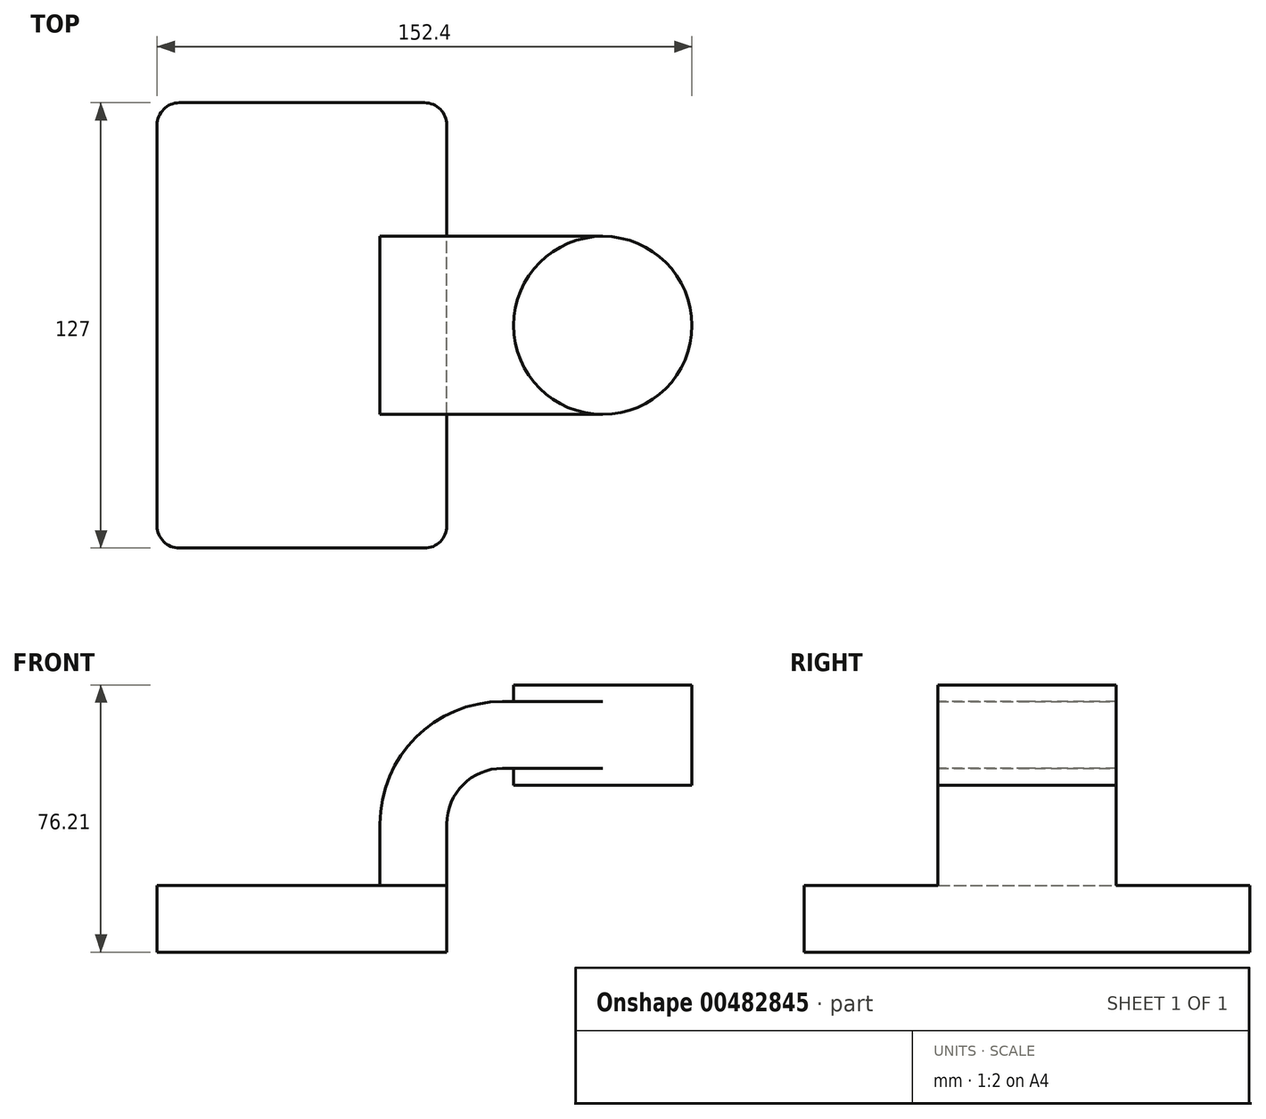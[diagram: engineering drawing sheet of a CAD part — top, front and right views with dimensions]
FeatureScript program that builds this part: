
annotation { "Feature Type Name" : "Feature", "Feature Type Description" : "" }
export const myFeature = defineFeature(function(context is Context, id is Id, definition is map)
    precondition{}
    {
        {
            var Q0;
            Q0=qCreatedBy(makeId("Front.planeOp"),FACE);
            var sketch = newSketch(context, id + "F0", { "sketchPlane" : qUnion([Q0])});
            skLineSegment(sketch, "E0.bottom", {"start": v(-41.28, -9.53) * mm, "end": v(41.28, -9.53) * mm});
            skLineSegment(sketch, "E0.top", {"start": v(-41.28, 9.53) * mm, "end": v(41.28, 9.53) * mm});
            skLineSegment(sketch, "E0.left", {"start": v(-41.28, -9.53) * mm, "end": v(-41.28, 9.53) * mm});
            skLineSegment(sketch, "E0.right", {"start": v(41.28, -9.53) * mm, "end": v(41.28, 9.53) * mm});
            skPoint(sketch, "E0.middle", {"position": v(0, 0) * mm});
            skLineSegment(sketch, "E1", {"start": v(41.27, 9.53) * mm, "end": v(41.27, 27) * mm});
            skLineSegment(sketch, "E2.bottom", {"start": v(60.32, 38.1) * mm, "end": v(111.12, 38.1) * mm});
            skLineSegment(sketch, "E2.top", {"start": v(60.32, 66.67) * mm, "end": v(111.12, 66.67) * mm});
            skLineSegment(sketch, "E2.left", {"start": v(60.32, 38.1) * mm, "end": v(60.32, 66.67) * mm});
            skLineSegment(sketch, "E2.right", {"start": v(111.12, 38.1) * mm, "end": v(111.12, 66.67) * mm});
            skPoint(sketch, "E2.middle", {"position": v(85.72, 52.39) * mm});
            skArc(sketch, "E3", {"start": v(41.27, 27) * mm, "mid": v(45.92, 38.23) * mm, "end": v(57.15, 42.88) * mm});
            skLineSegment(sketch, "E4", {"start": v(57.15, 42.88) * mm, "end": v(85.72, 42.88) * mm});
            skPoint(sketch, "E4.endSnap0", {"position": v(85.72, 38.1) * mm});
            skLineSegment(sketch, "E5.0", {"start": v(57.15, 61.93) * mm, "end": v(85.72, 61.93) * mm});
            skArc(sketch, "E5.1", {"start": v(22.22, 27) * mm, "mid": v(32.45, 51.7) * mm, "end": v(57.15, 61.93) * mm});
            skLineSegment(sketch, "E5.2", {"start": v(22.22, 9.53) * mm, "end": v(22.22, 27) * mm});
            skFitSpline(sketch, "E6", {"points": [v(-41.28, 9.53) * mm, v(57.15, 61.93) * mm], "startDerivative": vector(0.47, 82.14) * mm, "endDerivative": vector(124.84, -0.37) * mm});
            skLineSegment(sketch, "E7", {"start": v(85.72, 38.1) * mm, "end": v(85.72, 66.67) * mm});
            skSolve(sketch);
        }
        {
            var Q0;
            Q0=makeQuery(id+"F0.imprint","IMPRINT",FACE,{"disambiguationData":[TD([[makeQuery(id+"F0.imprint","IMPRINT",EDGE,{"derivedFrom":sQuery(id+"F0.wireOp",EDGE,"E0.bottom")}),1.0]])]});
            extrude(context, id + "F1", {"entities" : qUnion([Q0]), "endBound" : BoundingType.SYMMETRIC, "depth" : 127 * mm});
        }
        {
            var Q0;
            {var subQ5=sQuery(id+"F0.wireOp",EDGE,"E1");Q0=makeQuery(id+"F0.imprint","IMPRINT",FACE,{"disambiguationData":[TD([[makeQuery(id+"F0.imprint","IMPRINT",EDGE,{"derivedFrom":subQ5}),1.0]])]});}
            var Q1;
            {var subQ5=sQuery(id+"F0.wireOp",EDGE,"JxEZ6UGw-R51e-VeqM-CbXv-5OtBuTNwPAjv");Q1=makeQuery(id+"F0.imprint","IMPRINT",FACE,{"disambiguationData":[TD([[makeQuery(id+"F0.imprint","IMPRINT",EDGE,{"derivedFrom":subQ5}),1.0]])]});}
            extrude(context, id + "F2", {"entities" : qUnion([Q0, Q1]), "operationType" : NewBodyOperationType.ADD, "endBound" : BoundingType.SYMMETRIC, "depth" : 50.8 * mm});
        }
        {
            var Q0;
            Q0=makeQuery(id+"F0.imprint","IMPRINT",FACE,{"disambiguationData":[TD([[makeQuery(id+"F0.imprint","IMPRINT",EDGE,{"derivedFrom":sQuery(id+"F0.wireOp",EDGE,"E5.1")}),1.0]])]});
            extrude(context, id + "F3", {"entities" : qUnion([Q0]), "operationType" : NewBodyOperationType.ADD, "endBound" : BoundingType.SYMMETRIC, "depth" : 15.88 * mm});
        }
        {
            var Q0;
            {var subQ0=sQuery(id+"F0.wireOp",EDGE,"E4");var subQ1=sQuery(id+"F0.wireOp",EDGE,"E2.left");var subQ2=makeQuery(id+"F0.imprint","INTERSECT",VERTEX,{"derivedFrom":[subQ1,subQ0]});Q0=makeQuery(id+"F0.imprint","IMPRINT",FACE,{"disambiguationData":[TD([[makeQuery(id+"F0.imprint","IMPRINT",EDGE,{"disambiguationData":[TD([[subQ2,-1.0]])],"derivedFrom":subQ1}),-1.0]])]});}
            extrude(context, id + "F4", {"entities" : qUnion([Q0]), "operationType" : NewBodyOperationType.ADD, "endBound" : BoundingType.SYMMETRIC, "depth" : 50.8 * mm});
        }
        {
            var Q0;
            {var subQ0=sQuery(id+"F0.wireOp",EDGE,"E2.right");Q0=makeQuery(id+"F0.imprint","IMPRINT",FACE,{"disambiguationData":[TD([[makeQuery(id+"F0.imprint","IMPRINT",EDGE,{"derivedFrom":subQ0}),1.0]])]});}
            var Q1;
            Q1=sQuery(id+"F0.wireOp",EDGE,"E7");
            revolve(context, id + "F5", {"operationType" : NewBodyOperationType.ADD, "entities" : qUnion([Q0]), "axis" : qUnion([Q1]), "revolveType" : RevolveType.FULL});
        }
        {
            var Q0;
            Q0=makeQuery(id+"F1.opExtrude","CAP_EDGE",EDGE,{"disambiguationData":[OSD([sQuery(id+"F0.wireOp",EDGE,"E0.right")])],"isStart":false});
            var Q1;
            Q1=makeQuery(id+"F1.opExtrude","CAP_EDGE",EDGE,{"disambiguationData":[OSD([sQuery(id+"F0.wireOp",EDGE,"E0.left")])],"isStart":false});
            var Q2;
            Q2=makeQuery(id+"F1.opExtrude","CAP_EDGE",EDGE,{"disambiguationData":[OSD([sQuery(id+"F0.wireOp",EDGE,"E0.right")])],"isStart":true});
            var Q3;
            Q3=makeQuery(id+"F1.opExtrude","CAP_EDGE",EDGE,{"disambiguationData":[OSD([sQuery(id+"F0.wireOp",EDGE,"E0.left")])],"isStart":true});
            fillet(context, id + "F6", {"entities" : qUnion([Q0, Q1, Q2, Q3]), "radius" : 6.35 * mm, "tangentPropagation" : true, "allowEdgeOverflow" : false});
        }
    });
